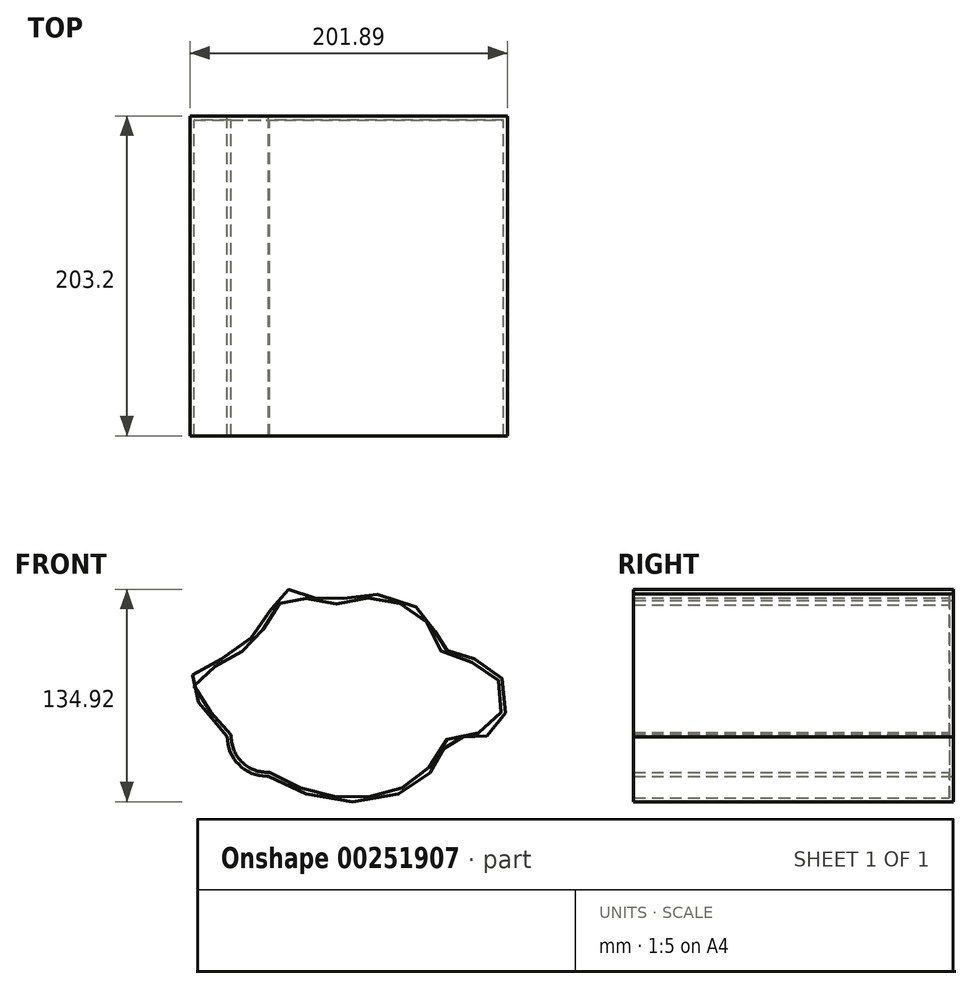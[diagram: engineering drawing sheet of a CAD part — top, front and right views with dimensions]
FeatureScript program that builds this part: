
annotation { "Feature Type Name" : "Feature", "Feature Type Description" : "" }
export const myFeature = defineFeature(function(context is Context, id is Id, definition is map)
    precondition{}
    {
        {
            var Q0;
            Q0=qCreatedBy(makeId("Front.planeOp"),FACE);
            var sketch = newSketch(context, id + "F0", { "sketchPlane" : qUnion([Q0])});
            skLineSegment(sketch, "E0.top", {"start": v(-14.1, -19.59) * mm, "end": v(-13.34, -19.59) * mm});
            skPoint(sketch, "E1.visualSharp", {"position": v(-39.5, 82.01) * mm});
            skPoint(sketch, "E2.visualSharp", {"position": v(112.9, 82.01) * mm});
            skPoint(sketch, "E3.visualSharp", {"position": v(112.9, -19.59) * mm});
            skPoint(sketch, "E4.visualSharp", {"position": v(-39.5, -19.59) * mm});
            skArc(sketch, "E4.filletArc", {"start": v(-39.5, 5.81) * mm, "mid": v(-32.06, -12.15) * mm, "end": v(-14.1, -19.59) * mm});
            skFitSpline(sketch, "E5", {"points": [v(-39.5, 5.81) * mm, v(-63.05, 41.48) * mm, v(-39.5, 56.61) * mm, v(-14.1, 82.01) * mm, v(0, 99.14) * mm, v(21.57, 92.1) * mm, v(48.53, 96.24) * mm, v(87.5, 82.01) * mm, v(96.24, 63.47) * mm, v(112.9, 56.61) * mm, v(137.72, 37.33) * mm, v(129.01, 7.88) * mm, v(112.9, 5.81) * mm, v(99.56, 0) * mm, v(87.5, -19.59) * mm, v(38.58, -35.67) * mm, v(-14.1, -19.08) * mm, v(-39.5, 5.81) * mm]});
            skSolve(sketch);
        }
        {
            var Q0;
            Q0 = qSketchRegion(id + "F0", true);
            extrude(context, id + "F1", {"entities" : qUnion([Q0]), "depth" : 76.2 * mm, "hasSecondDirection" : true, "secondDirectionOppositeDirection" : true, "secondDirectionDepth" : 127 * mm});
        }
        {
            var Q0;
            Q0=makeQuery(id+"F1.opExtrude","CAP_FACE",FACE,{"disambiguationData":[OSD([sQuery(id+"F0.wireOp",EDGE,"E0.top"),sQuery(id+"F0.wireOp",EDGE,"E4.filletArc"),sQuery(id+"F0.wireOp",EDGE,"E5")])],"isStart":false});
            shell(context, id + "F2", {"entities" : qUnion([Q0]), "thickness" : 2.54 * mm});
        }
    });
